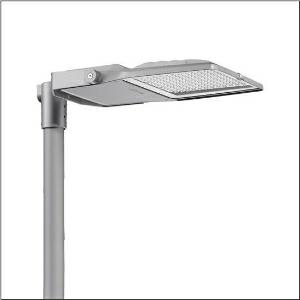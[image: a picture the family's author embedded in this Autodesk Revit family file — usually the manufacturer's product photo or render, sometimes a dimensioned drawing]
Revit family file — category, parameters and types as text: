
# Revit family: floodlight_fl_21_midi___pl33t_5xa7785e2f3a_9b27
name_source: partatom
category: Lighting Fixtures
units: mm (PartAtom-declared; Revit-internal decimal feet)

## family parameters
Cut with Voids When Loaded = No
Host = Face
Light Source = No
Part Type = Normal
Room Calculation Point = No
Round Connector Dimension = Use Diameter
Shared = No

## types (1)
- --- (1 x LED, 26630 lm, 212.4 W, 3000K)
    Apparent Load = 212 VA
    CIE Flux Codes = 26 75 99 100 100
    Color Rendering = 70
    Color Temperature = 3000K
    Default Elevation = 1800 mm
    Description = Floodlight FL 21 midi, floodlight, primary light control with lens, of PMMA, primary optical cover: protective disc, of toughened safety glass, transparent, light distribution: PL33T, light emission: direct distribution, installation type: surface-mounted, LED, High Power LED, rated luminous flux: 26.630lm, luminous efficacy: 125lm/W, light colour: 730, colour temperature: 3000K, control gear: Smart Interface (Zhaga), control: flexible luminous flux parameterisation, time-dependent luminous flux control, constant luminous flux control, overheat protection, pre-setting: logarithmic dimming characteristic, with terminal, 6-pole, mains connection: 220..240V, AC, 50/60Hz, start of lifetime: 212W, end of service life: 231W, reduction: 95W, luminaire housing, of diecast aluminium, powder-coated, SITECO metallic grey (DB 702S), corrosivity category C5 mid according to DIN EN ISO 12944, suitable for swimming pools, chlorine-resistant, sealing non-destructively replaceable, please order mast flange separately, mast bracket, of steel, galvanised, powder-coated, SITECO metallic grey (DB 702S), Smart Interface above, protection rating (complete): IP66, insulation class (complete): insulation class II (safety insulation), certification: CE, ENEC, VDE, protection symbol: D, impact resistance: IK08, permissible operating ambient temperature: -20..+40°C, permissible operating ambient temperature for outdoor applications: -40..+50°C, standard: DIN EN 12944, LABS conformity tested according to VDMA 24364:2018-05, packaging unit: 1 piece

Light Distribution: PL33T
    Height = 76 mm
    Lamp = 1 x LED
    Lamp Light Flux = 26630 lm
    Lamp Power = 212.4 W
    Lamp count = 1
    Length = 657 mm
    Luminous efficacy = 125 lm/W
    Manufacturer = Siteco
    ModVariant = No
    Model = 5XA7785E2F3A
    Number of Poles = 1
    OnlyDefault = Yes
    Power Factor = 1
    Product Name = Floodlight FL 21 midi | PL33T
    Product group = floodlight | pylon annexe
    ProductGroupID = 6201
    Protection Class = Protection class II
    Protection Degree = IP 66
    RLX_Detail_Level = 1
    RLX_Emergency_Light_Flux = 0 lm
    RLX_Emergency_Type = 0
    RLX_Emergency_Type_DB = No
    RlxData = <blob elided: 153585 chars, md5=0526b6ef>
    Socket = socket
    Standby Power = 0 W
    System Light Flux = 26630 lm
    System Power = 212 W
    Type Comments = factory setting: luminous flux: 100 % | dim-lin: 254 | 710 mA
    Type Image = l_1007123.jpg
    URL = http://relux.com
    VarID = @adj_150115
    Voltage = 0 V
    Weight = 0.00 kg
    Width = 442 mm

## geometry (parser evidence)
native form markers: Blend x4, Sweep x14
no freeform markers — native parametric forms only
